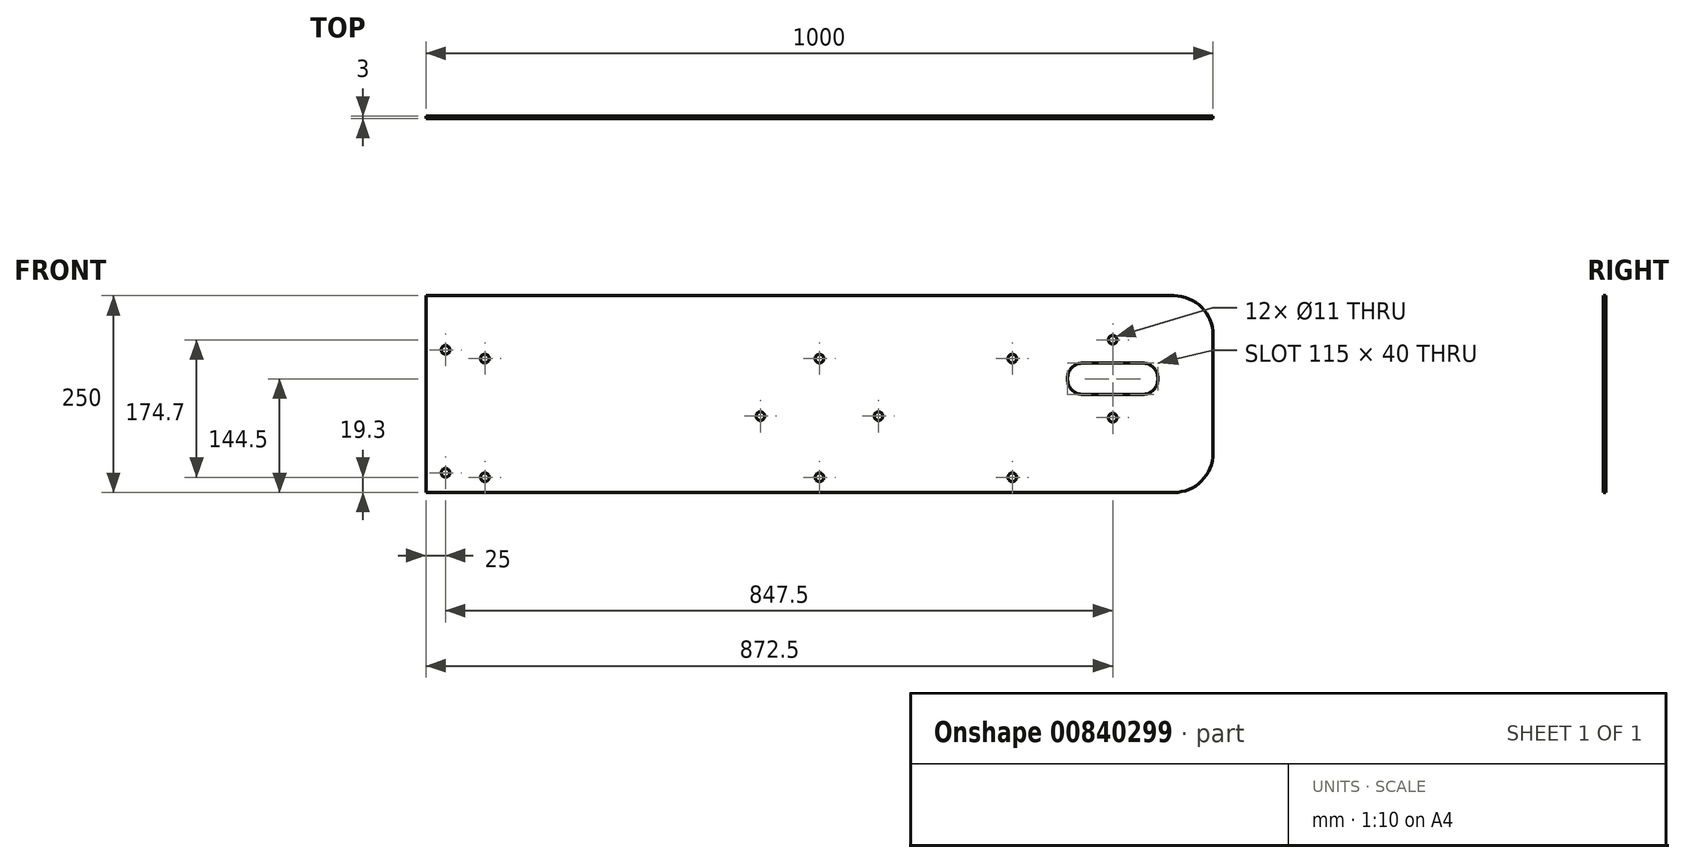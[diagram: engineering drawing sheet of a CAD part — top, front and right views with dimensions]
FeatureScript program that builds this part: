
annotation { "Feature Type Name" : "Feature", "Feature Type Description" : "" }
export const myFeature = defineFeature(function(context is Context, id is Id, definition is map)
    precondition{}
    {
        {
            var Q0;
            Q0=qCreatedBy(makeId("Front.planeOp"),FACE);
            var sketch = newSketch(context, id + "F0", { "sketchPlane" : qUnion([Q0])});
            skLineSegment(sketch, "E0.bottom", {"start": v(-500, 125) * mm, "end": v(500, 125) * mm});
            skLineSegment(sketch, "E0.top", {"start": v(-500, -125) * mm, "end": v(500, -125) * mm});
            skLineSegment(sketch, "E0.left", {"start": v(-500, 125) * mm, "end": v(-500, -125) * mm});
            skLineSegment(sketch, "E0.right", {"start": v(500, 125) * mm, "end": v(500, -125) * mm});
            skPoint(sketch, "E0.middle", {"position": v(0, 0) * mm});
            skSolve(sketch);
        }
        {
            var Q0;
            Q0 = qSketchRegion(id + "F0", true);
            extrude(context, id + "F1", {"entities" : qUnion([Q0]), "endBound" : BoundingType.SYMMETRIC, "depth" : 3 * mm, "offsetDistance" : 25 * mm});
        }
        {
            var Q0;
            Q0=makeQuery(id+"F1.opExtrude","CAP_FACE",FACE,{"disambiguationData":[OSD([sQuery(id+"F0.wireOp",EDGE,"E0.bottom"),sQuery(id+"F0.wireOp",EDGE,"E0.top"),sQuery(id+"F0.wireOp",EDGE,"E0.left"),sQuery(id+"F0.wireOp",EDGE,"E0.right")])],"isStart":false});
            var sketch = newSketch(context, id + "F2", { "sketchPlane" : qUnion([Q0])});
            skPoint(sketch, "E1", {"position": v(-475, -100) * mm});
            skPoint(sketch, "E2", {"position": v(-475, 56.2) * mm});
            skPoint(sketch, "E3", {"position": v(-425, -105.7) * mm});
            skPoint(sketch, "E4", {"position": v(-425, 45.1) * mm});
            skPoint(sketch, "E5", {"position": v(-75, -28) * mm});
            skPoint(sketch, "E6", {"position": v(75, -28) * mm});
            skPoint(sketch, "E7", {"position": v(0, 45.1) * mm});
            skPoint(sketch, "E8", {"position": v(0, -105.7) * mm});
            skPoint(sketch, "E9", {"position": v(245, 45.1) * mm});
            skPoint(sketch, "E10", {"position": v(245, -105.7) * mm});
            skSolve(sketch);
        }
        {
            var Q0;
            Q0=sQuery(id+"F2.wireOp",VERTEX,"E2");
            var Q1;
            Q1=sQuery(id+"F2.wireOp",VERTEX,"E1");
            var Q2;
            Q2=sQuery(id+"F2.wireOp",VERTEX,"E3");
            var Q3;
            Q3=sQuery(id+"F2.wireOp",VERTEX,"E4");
            var Q4;
            Q4=sQuery(id+"F2.wireOp",VERTEX,"E5");
            var Q5;
            Q5=sQuery(id+"F2.wireOp",VERTEX,"E6");
            var Q6;
            Q6=sQuery(id+"F2.wireOp",VERTEX,"E8");
            var Q7;
            Q7=sQuery(id+"F2.wireOp",VERTEX,"E7");
            var Q8;
            Q8=sQuery(id+"F2.wireOp",VERTEX,"E9");
            var Q9;
            Q9=sQuery(id+"F2.wireOp",VERTEX,"E10");
            var Q10;
            Q10=makeQuery(id+"F1.opExtrude","SWEPT_BODY",BODY,{"disambiguationData":[OSD([sQuery(id+"F0.wireOp",EDGE,"E0.bottom"),sQuery(id+"F0.wireOp",EDGE,"E0.top"),sQuery(id+"F0.wireOp",EDGE,"E0.left"),sQuery(id+"F0.wireOp",EDGE,"E0.right")])]});
            hole(context, id + "F3", {"style" : HoleStyle.SIMPLE, "endStyle" : HoleEndStyle.BLIND, "standardTappedOrClearance" : lookupTablePath({ "fit" : "Normal", "standard" : "ISO", "size" : "M10", "type" : "Clearance" }), "standardBlindInLast" : lookupTablePath({ "fit" : "Standard", "standard" : "ISO", "size" : "M10", "type" : "Clearance" }), "holeDiameter" : 11 * mm, "majorDiameter" : 16 * mm, "holeDepth" : 18 * mm, "isTappedThrough" : true, "tappedDepth" : 12 * mm, "tapClearance" : 3, "startFromSketch" : true, "locations" : qUnion([Q0, Q1, Q2, Q3, Q4, Q5, Q6, Q7, Q8, Q9]), "scope" : qUnion([Q10])});
        }
        {
            var Q0;
            Q0=makeQuery(id+"F1.opExtrude","CAP_FACE",FACE,{"disambiguationData":[OSD([sQuery(id+"F0.wireOp",EDGE,"E0.bottom"),sQuery(id+"F0.wireOp",EDGE,"E0.top"),sQuery(id+"F0.wireOp",EDGE,"E0.left"),sQuery(id+"F0.wireOp",EDGE,"E0.right")])],"isStart":true});
            var sketch = newSketch(context, id + "F4", { "sketchPlane" : qUnion([Q0])});
            skCircle(sketch, "E11", {"center": v(-372.5, -30) * mm, "radius": 5.5 * mm});
            skCircle(sketch, "E12", {"center": v(-372.5, 69) * mm, "radius": 5.5 * mm});
            skLineSegment(sketch, "E13", {"start": v(-410, 19.5) * mm, "end": v(-335, 19.5) * mm});
            skLineSegment(sketch, "E14", {"start": v(-372.5, 19.5) * mm, "end": v(-372.5, 69) * mm, "construction": true});
            skArc(sketch, "E15.0.startCap", {"start": v(-410, -0.5) * mm, "mid": v(-430, 19.5) * mm, "end": v(-410, 39.5) * mm});
            skArc(sketch, "E15.0.endCap", {"start": v(-335, 39.5) * mm, "mid": v(-315, 19.5) * mm, "end": v(-335, -0.5) * mm});
            skLineSegment(sketch, "E15.0.left", {"start": v(-410, 39.5) * mm, "end": v(-335, 39.5) * mm});
            skLineSegment(sketch, "E15.0.right", {"start": v(-410, -0.5) * mm, "end": v(-335, -0.5) * mm});
            skSolve(sketch);
        }
        {
            var Q0;
            Q0 = qSketchRegion(id + "F4", true);
            extrude(context, id + "F5", {"entities" : qUnion([Q0]), "operationType" : NewBodyOperationType.REMOVE, "endBound" : BoundingType.THROUGH_ALL, "oppositeDirection" : true, "depth" : 25 * mm, "offsetDistance" : 25 * mm});
        }
        {
            var Q0;
            Q0=makeQuery(id+"F1.opExtrude","SWEPT_EDGE",EDGE,{"disambiguationData":[OSD([sQuery(id+"F0.wireOp",EDGE,"E0.bottom"),sQuery(id+"F0.wireOp",EDGE,"E0.right")])]});
            var Q1;
            Q1=makeQuery(id+"F1.opExtrude","SWEPT_EDGE",EDGE,{"disambiguationData":[OSD([sQuery(id+"F0.wireOp",EDGE,"E0.top"),sQuery(id+"F0.wireOp",EDGE,"E0.right")])]});
            fillet(context, id + "F6", {"entities" : qUnion([Q0, Q1]), "radius" : 50 * mm, "tangentPropagation" : true, "allowEdgeOverflow" : false});
        }
    });
